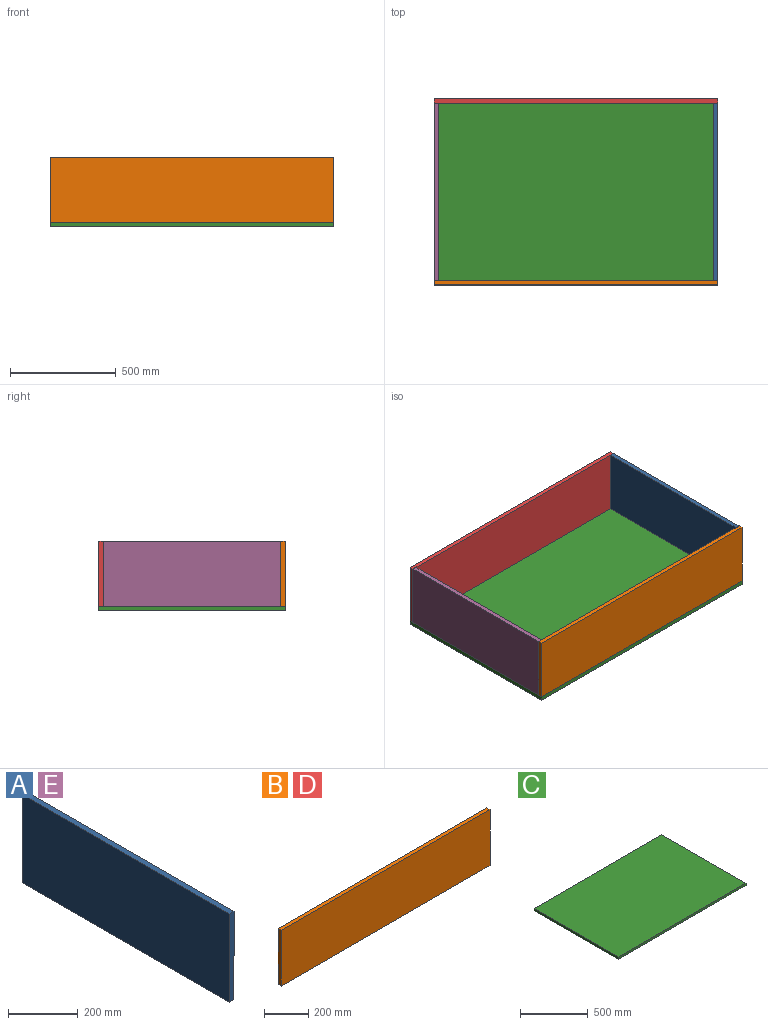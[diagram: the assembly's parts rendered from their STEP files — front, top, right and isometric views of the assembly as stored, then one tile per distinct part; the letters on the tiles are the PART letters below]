
ASSEMBLY  parts=5 mates=10
PART A: 6 faces, bbox 20x840x310 mm
  f0: plane 310x20mm, normal (0,-1,0), area 6200mm2, adj f1,f3,f4,f5
  f1: plane 840x20mm, normal (0,0,-1), area 16800mm2, adj f0,f2,f4,f5
  f2: plane 310x20mm, normal (0,1,0), area 6200mm2, adj f1,f3,f4,f5
  f3: plane 840x20mm, normal (0,0,1), area 16800mm2, adj f0,f2,f4,f5
  f4: plane 840x310mm, normal (1,0,0), area 260400mm2, adj f0,f1,f2,f3
  f5: plane 840x310mm, normal (-1,0,0), area 260400mm2, adj f0,f1,f2,f3
PART B: 6 faces, bbox 1340x20x310 mm
  f0: plane 310x20mm, normal (-1,0,0), area 6200mm2, adj f1,f3,f4,f5
  f1: plane 1340x20mm, normal (0,0,-1), area 26800mm2, adj f0,f2,f4,f5
  f2: plane 310x20mm, normal (1,0,0), area 6200mm2, adj f1,f3,f4,f5
  f3: plane 1340x20mm, normal (0,0,1), area 26800mm2, adj f0,f2,f4,f5
  f4: plane 1340x310mm, normal (0,-1,0), area 415400mm2, adj f0,f1,f2,f3
  f5: plane 1340x310mm, normal (0,1,0), area 415400mm2, adj f0,f1,f2,f3
PART C: 6 faces, bbox 1340x880x20 mm
  f0: plane 880x20mm, normal (-1,0,0), area 17600mm2, adj f1,f3,f4,f5
  f1: plane 1340x20mm, normal (0,-1,0), area 26800mm2, adj f0,f2,f4,f5
  f2: plane 880x20mm, normal (1,0,0), area 17600mm2, adj f1,f3,f4,f5
  f3: plane 1340x20mm, normal (0,1,0), area 26800mm2, adj f0,f2,f4,f5
  f4: plane 1340x880mm, normal (0,0,1), area 1179200mm2, adj f0,f1,f2,f3
  f5: plane 1340x880mm, normal (0,0,-1), area 1179200mm2, adj f0,f1,f2,f3
PART D: same geometry as B
PART E: same geometry as A
PLACE A t=(650,-420,20)mm
PLACE B t=(-670,-420,20)mm
PLACE C rot(axis=(0,0,1),180deg) t=(670,440,0)mm
PLACE D t=(-670,440,20)mm
PLACE E t=(-670,-420,20)mm
MATE planar A.f4 <-> B.f2  axis (1,0,0) through (670,-420,175)mm
MATE fastened A.f4 <-> D.f2  axis (1,0,0) through (670,420,175)mm
MATE planar B.f5 <-> A.f0  axis (0,1,0) through (670,-420,175)mm
MATE planar A.f3 <-> D.f3  axis (0,0,1) through (670,420,330)mm
MATE fastened E.f5 <-> B.f0  axis (-1,0,0) through (-670,-420,175)mm
MATE fastened B.f1 <-> C.f4  axis (0,0,-1) through (-670,-440,20)mm
MATE planar A.f0 <-> E.f0  axis (0,-1,0) through (660,-420,175)mm
MATE planar A.f4 <-> D.f2  axis (1,0,0) through (670,420,175)mm
MATE planar E.f5 <-> B.f0  axis (-1,0,0) through (-670,-420,175)mm
MATE planar B.f3 <-> A.f3  axis (0,0,1) through (670,-420,330)mm
